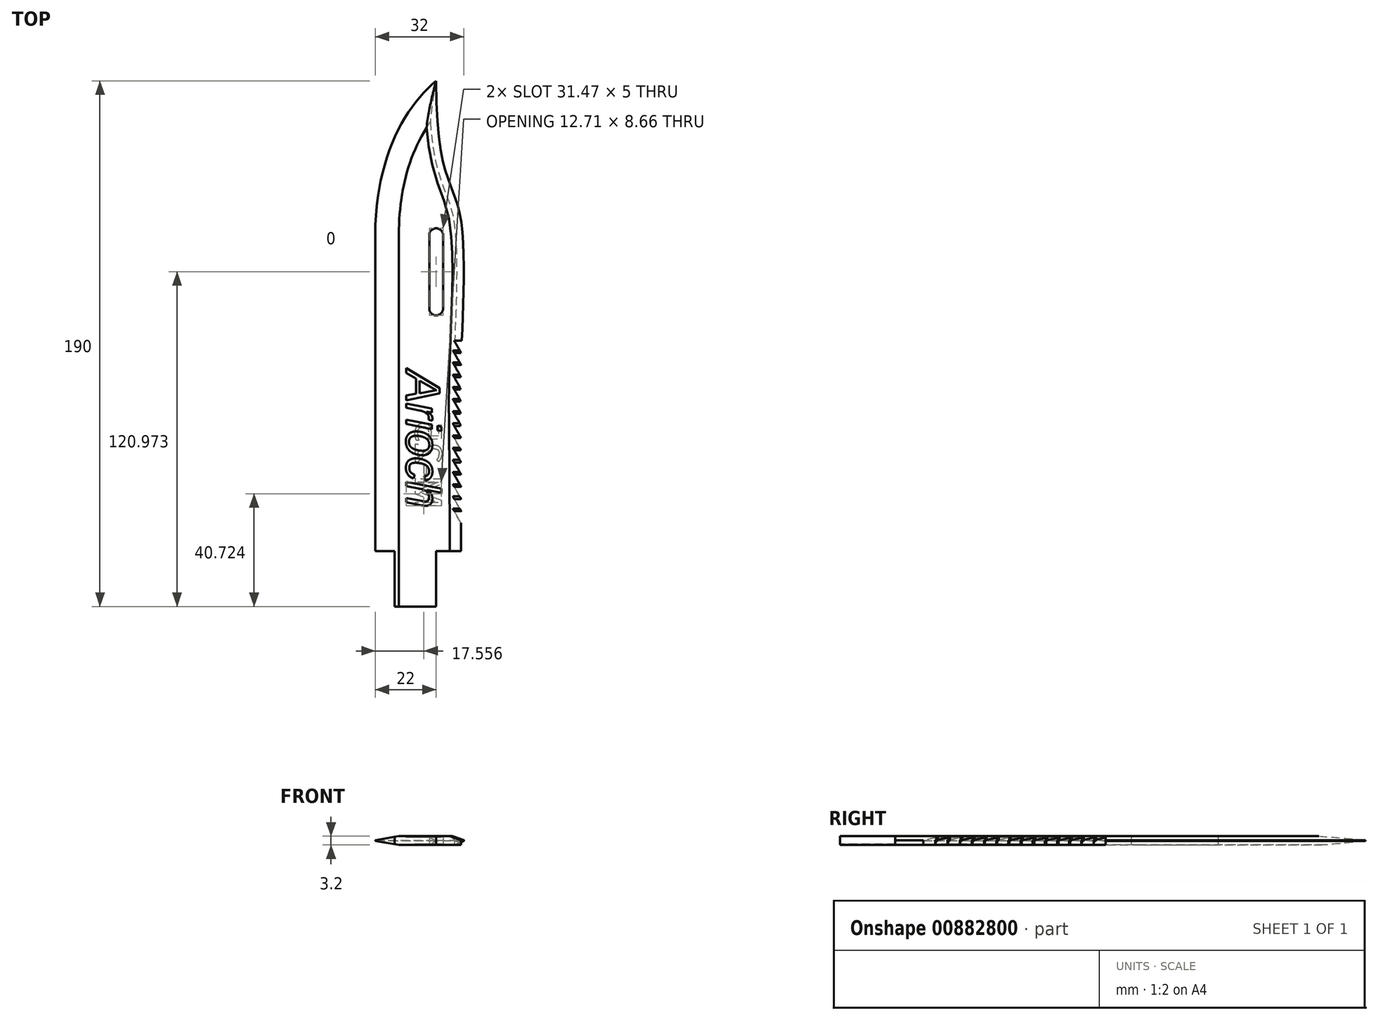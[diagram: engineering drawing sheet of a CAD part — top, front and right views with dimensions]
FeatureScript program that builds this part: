
annotation { "Feature Type Name" : "Feature", "Feature Type Description" : "" }
export const myFeature = defineFeature(function(context is Context, id is Id, definition is map)
    precondition{}
    {
        {
            var Q0;
            Q0=qCreatedBy(makeId("Top.planeOp"),FACE);
            var sketch = newSketch(context, id + "F0", { "sketchPlane" : qUnion([Q0])});
            skLineSegment(sketch, "E0", {"start": v(0, 138.73) * mm, "end": v(0, -81.27) * mm, "construction": true});
            skLineSegment(sketch, "E1", {"start": v(-22, -31.27) * mm, "end": v(9, -31.27) * mm, "construction": true});
            skLineSegment(sketch, "E2", {"start": v(-15, -31.27) * mm, "end": v(-15, -79.27) * mm});
            skLineSegment(sketch, "E3", {"start": v(0, -31.27) * mm, "end": v(0, -78.27) * mm});
            skLineSegment(sketch, "E4", {"start": v(-13, -81.27) * mm, "end": v(-3, -81.27) * mm});
            skPoint(sketch, "E5.visualSharp", {"position": v(0, -81.27) * mm});
            skArc(sketch, "E5.filletArc", {"start": v(-3, -81.27) * mm, "mid": v(-0.88, -80.39) * mm, "end": v(0, -78.27) * mm});
            skPoint(sketch, "E6.visualSharp", {"position": v(-15, -81.27) * mm});
            skArc(sketch, "E6.filletArc", {"start": v(-15, -79.27) * mm, "mid": v(-14.41, -80.68) * mm, "end": v(-13, -81.27) * mm});
            skLineSegment(sketch, "E7", {"start": v(9, -31.27) * mm, "end": v(9, 122.8) * mm, "construction": true});
            skLineSegment(sketch, "E8", {"start": v(-22, -31.27) * mm, "end": v(-22, 123.89) * mm, "construction": true});
            skLineSegment(sketch, "E9", {"start": v(-15, -31.27) * mm, "end": v(-22, -31.27) * mm});
            skLineSegment(sketch, "E10", {"start": v(0, -31.27) * mm, "end": v(9, -31.27) * mm});
            skLineSegment(sketch, "E11", {"start": v(-22, -31.27) * mm, "end": v(-22, 83.23) * mm});
            skFitSpline(sketch, "E12", {"points": [v(-22, 83.23) * mm, v(0, 138.73) * mm], "startDerivative": vector(0, 80.42) * mm, "endDerivative": vector(35.05, 28.76) * mm});
            skFitSpline(sketch, "E13", {"points": [v(0, 138.73) * mm, v(8.64, 90.14) * mm, v(9, 37.85) * mm, v(9, -31.27) * mm], "startDerivative": vector(0, -335.88) * mm, "endDerivative": vector(0, -393.77) * mm});
            skLineSegment(sketch, "E14", {"start": v(-8, -81.27) * mm, "end": v(-8, -31.27) * mm, "construction": true});
            skSolve(sketch);
        }
        {
            var Q0;
            Q0=qSketchRegion(id+"F0",true);
            extrude(context, id + "F1", {"entities" : qUnion([Q0]), "depth" : 3.2 * mm, "offsetDistance" : 25.4 * mm});
        }
        {
            var Q0;
            Q0=makeQuery(id+"F1.opExtrude","CAP_EDGE",EDGE,{"disambiguationData":[OSD([sQuery(id+"F0.wireOp",EDGE,"E11")])],"isStart":false});
            var Q1;
            Q1=makeQuery(id+"F1.opExtrude","CAP_EDGE",EDGE,{"disambiguationData":[OSD([sQuery(id+"F0.wireOp",EDGE,"E12")])],"isStart":false});
            chamfer(context, id + "F2", {"entities" : qUnion([Q0, Q1]), "chamferType" : ChamferType.OFFSET_ANGLE, "width" : 1.5 * mm, "oppositeDirection" : false, "angle" : 80 * degree, "tangentPropagation" : true});
        }
        {
            var Q0;
            Q0=makeQuery(id+"F1.opExtrude","CAP_EDGE",EDGE,{"disambiguationData":[OSD([sQuery(id+"F0.wireOp",EDGE,"E12")])],"isStart":true});
            chamfer(context, id + "F3", {"entities" : qUnion([Q0]), "chamferType" : ChamferType.OFFSET_ANGLE, "width" : 1.5 * mm, "oppositeDirection" : true, "angle" : 80 * degree, "tangentPropagation" : true});
        }
        {
            var Q0;
            Q0=makeQuery(id+"F1.opExtrude","CAP_FACE",FACE,{"disambiguationData":[OSD([sQuery(id+"F0.wireOp",EDGE,"E2"),sQuery(id+"F0.wireOp",EDGE,"E3"),sQuery(id+"F0.wireOp",EDGE,"E4"),sQuery(id+"F0.wireOp",EDGE,"E5.filletArc"),sQuery(id+"F0.wireOp",EDGE,"E6.filletArc"),sQuery(id+"F0.wireOp",EDGE,"E9"),sQuery(id+"F0.wireOp",EDGE,"E10"),sQuery(id+"F0.wireOp",EDGE,"E11"),sQuery(id+"F0.wireOp",EDGE,"E12"),sQuery(id+"F0.wireOp",EDGE,"E13")])],"isStart":true});
            var sketch = newSketch(context, id + "F4", { "sketchPlane" : qUnion([Q0])});
            skSolve(sketch);
        }
        {
            var Q0;
            {var subQ3=sQuery(id+"F0.wireOp",EDGE,"E10");Q0=makeQuery(id+"F4.imprint","IMPRINT",FACE,{"disambiguationData":[TD([[makeQuery(id+"F4.imprint","IMPRINT",EDGE,{"derivedFrom":makeQuery(id+"F1.opExtrude","CAP_EDGE",EDGE,{"disambiguationData":[OSD([subQ3])],"isStart":true})}),-1.0]])]});}
            var sketch = newSketch(context, id + "F5", { "sketchPlane" : qUnion([Q0])});
            skLineSegment(sketch, "E15", {"start": v(10.09, 23.07) * mm, "end": v(6.53, 16.8) * mm});
            skLineSegment(sketch, "E16", {"start": v(6.53, 16.8) * mm, "end": v(10.43, 16.8) * mm});
            skLineSegment(sketch, "E17", {"start": v(10.09, 23.07) * mm, "end": v(10.43, 16.8) * mm});
            skLineSegment(sketch, "E18.0.1.0", {"start": v(10.09, 18.67) * mm, "end": v(10.43, 12.4) * mm});
            skLineSegment(sketch, "E18.0.1.1", {"start": v(6.53, 12.4) * mm, "end": v(10.43, 12.4) * mm});
            skLineSegment(sketch, "E18.0.1.2", {"start": v(10.09, 18.67) * mm, "end": v(6.53, 12.4) * mm});
            skLineSegment(sketch, "E18.0.2.0", {"start": v(10.09, 14.27) * mm, "end": v(10.43, 8) * mm});
            skLineSegment(sketch, "E18.0.2.1", {"start": v(6.53, 8) * mm, "end": v(10.43, 8) * mm});
            skLineSegment(sketch, "E18.0.2.2", {"start": v(10.09, 14.27) * mm, "end": v(6.53, 8) * mm});
            skLineSegment(sketch, "E18.0.3.0", {"start": v(10.09, 9.87) * mm, "end": v(10.43, 3.6) * mm});
            skLineSegment(sketch, "E18.0.3.1", {"start": v(6.53, 3.6) * mm, "end": v(10.43, 3.6) * mm});
            skLineSegment(sketch, "E18.0.3.2", {"start": v(10.09, 9.87) * mm, "end": v(6.53, 3.6) * mm});
            skLineSegment(sketch, "E18.0.4.0", {"start": v(10.09, 5.47) * mm, "end": v(10.43, -0.8) * mm});
            skLineSegment(sketch, "E18.0.4.1", {"start": v(6.53, -0.8) * mm, "end": v(10.43, -0.8) * mm});
            skLineSegment(sketch, "E18.0.4.2", {"start": v(10.09, 5.47) * mm, "end": v(6.53, -0.8) * mm});
            skLineSegment(sketch, "E18.0.5.0", {"start": v(10.09, 1.07) * mm, "end": v(10.43, -5.2) * mm});
            skLineSegment(sketch, "E18.0.5.1", {"start": v(6.53, -5.2) * mm, "end": v(10.43, -5.2) * mm});
            skLineSegment(sketch, "E18.0.5.2", {"start": v(10.09, 1.07) * mm, "end": v(6.53, -5.2) * mm});
            skLineSegment(sketch, "E18.0.6.0", {"start": v(10.09, -3.33) * mm, "end": v(10.43, -9.6) * mm});
            skLineSegment(sketch, "E18.0.6.1", {"start": v(6.53, -9.6) * mm, "end": v(10.43, -9.6) * mm});
            skLineSegment(sketch, "E18.0.6.2", {"start": v(10.09, -3.33) * mm, "end": v(6.53, -9.6) * mm});
            skLineSegment(sketch, "E18.0.7.0", {"start": v(10.09, -7.73) * mm, "end": v(10.43, -14) * mm});
            skLineSegment(sketch, "E18.0.7.1", {"start": v(6.53, -14) * mm, "end": v(10.43, -14) * mm});
            skLineSegment(sketch, "E18.0.7.2", {"start": v(10.09, -7.73) * mm, "end": v(6.53, -14) * mm});
            skLineSegment(sketch, "E18.0.8.0", {"start": v(10.09, -12.13) * mm, "end": v(10.43, -18.4) * mm});
            skLineSegment(sketch, "E18.0.8.1", {"start": v(6.53, -18.4) * mm, "end": v(10.43, -18.4) * mm});
            skLineSegment(sketch, "E18.0.8.2", {"start": v(10.09, -12.13) * mm, "end": v(6.53, -18.4) * mm});
            skLineSegment(sketch, "E18.0.9.0", {"start": v(10.09, -16.53) * mm, "end": v(10.43, -22.8) * mm});
            skLineSegment(sketch, "E18.0.9.1", {"start": v(6.53, -22.8) * mm, "end": v(10.43, -22.8) * mm});
            skLineSegment(sketch, "E18.0.9.2", {"start": v(10.09, -16.53) * mm, "end": v(6.53, -22.8) * mm});
            skLineSegment(sketch, "E18.direction1", {"start": v(6.53, 16.8) * mm, "end": v(32.82, 16.8) * mm, "construction": true});
            skLineSegment(sketch, "E18.direction2", {"start": v(6.53, 16.8) * mm, "end": v(6.53, 12.4) * mm, "construction": true});
            skLineSegment(sketch, "E19.0.0.10", {"start": v(10.09, -20.93) * mm, "end": v(10.43, -27.2) * mm});
            skLineSegment(sketch, "E19.3.0.10", {"start": v(6.53, -27.2) * mm, "end": v(10.43, -27.2) * mm});
            skLineSegment(sketch, "E19.6.0.10", {"start": v(10.09, -20.93) * mm, "end": v(6.53, -27.2) * mm});
            skLineSegment(sketch, "E19.0.0.11", {"start": v(10.09, -25.33) * mm, "end": v(10.43, -31.6) * mm});
            skLineSegment(sketch, "E19.3.0.11", {"start": v(6.53, -31.6) * mm, "end": v(10.43, -31.6) * mm});
            skLineSegment(sketch, "E19.6.0.11", {"start": v(10.09, -25.33) * mm, "end": v(6.53, -31.6) * mm});
            skLineSegment(sketch, "E19.0.0.12", {"start": v(10.09, -29.73) * mm, "end": v(10.43, -36) * mm});
            skLineSegment(sketch, "E19.3.0.12", {"start": v(6.53, -36) * mm, "end": v(10.43, -36) * mm});
            skLineSegment(sketch, "E19.6.0.12", {"start": v(10.09, -29.73) * mm, "end": v(6.53, -36) * mm});
            skLineSegment(sketch, "E19.0.0.13", {"start": v(10.09, -34.13) * mm, "end": v(10.43, -40.4) * mm});
            skLineSegment(sketch, "E19.3.0.13", {"start": v(6.53, -40.4) * mm, "end": v(10.43, -40.4) * mm});
            skLineSegment(sketch, "E19.6.0.13", {"start": v(10.09, -34.13) * mm, "end": v(6.53, -40.4) * mm});
            skLineSegment(sketch, "E19.0.0.14", {"start": v(10.09, -38.53) * mm, "end": v(10.43, -44.8) * mm});
            skLineSegment(sketch, "E19.3.0.14", {"start": v(6.53, -44.8) * mm, "end": v(10.43, -44.8) * mm});
            skLineSegment(sketch, "E19.6.0.14", {"start": v(10.09, -38.53) * mm, "end": v(6.53, -44.8) * mm});
            skSolve(sketch);
        }
        {
            var Q0;
            Q0=qSketchRegion(id+"F5",true);
            extrude(context, id + "F6", {"entities" : qUnion([Q0]), "operationType" : NewBodyOperationType.REMOVE, "oppositeDirection" : true, "depth" : 25 * mm, "offsetDistance" : 25 * mm});
        }
        {
            var Q0;
            {var subQ3=sQuery(id+"F0.wireOp",EDGE,"E10");Q0=makeQuery(id+"F4.imprint","IMPRINT",FACE,{"disambiguationData":[TD([[makeQuery(id+"F4.imprint","IMPRINT",EDGE,{"derivedFrom":makeQuery(id+"F1.opExtrude","CAP_EDGE",EDGE,{"disambiguationData":[OSD([subQ3])],"isStart":true})}),-1.0]])]});}
            var sketch = newSketch(context, id + "F7", { "sketchPlane" : qUnion([Q0])});
            skLineSegment(sketch, "E20", {"start": v(0, -56.47) * mm, "end": v(0, -82.94) * mm, "construction": true});
            skArc(sketch, "E21.0.startCap", {"start": v(-2.5, -56.47) * mm, "mid": v(0, -53.97) * mm, "end": v(2.5, -56.47) * mm});
            skArc(sketch, "E21.0.endCap", {"start": v(2.5, -82.94) * mm, "mid": v(0, -85.44) * mm, "end": v(-2.5, -82.94) * mm});
            skLineSegment(sketch, "E21.0.left", {"start": v(2.5, -56.47) * mm, "end": v(2.5, -82.94) * mm});
            skLineSegment(sketch, "E21.0.right", {"start": v(-2.5, -56.47) * mm, "end": v(-2.5, -82.94) * mm});
            skSolve(sketch);
        }
        {
            var Q0;
            Q0=qSketchRegion(id+"F7",true);
            extrude(context, id + "F8", {"entities" : qUnion([Q0]), "operationType" : NewBodyOperationType.REMOVE, "oppositeDirection" : true, "depth" : 25 * mm, "offsetDistance" : 25 * mm});
        }
        {
            var Q0;
            {var subQ0=sQuery(id+"F0.wireOp",EDGE,"E13");var subQ1=sQuery(id+"F0.wireOp",EDGE,"E12");Q0=makeQuery(id+"F6.boolean.opBoolean","SPLIT",EDGE,{"disambiguationData":[TD([makeQuery(id+"F3.opChamfer","BLEND_FACE",FACE,{"disambiguationData":[OSD([subQ1])]})])],"derivedFrom":makeQuery(id+"F1.opExtrude","CAP_EDGE",EDGE,{"disambiguationData":[OSD([subQ0])],"isStart":true})});}
            chamfer(context, id + "F9", {"entities" : qUnion([Q0]), "chamferType" : ChamferType.OFFSET_ANGLE, "width" : 1.5 * mm, "oppositeDirection" : true, "angle" : 60 * degree, "tangentPropagation" : true});
        }
        {
            var Q0;
            {var subQ0=sQuery(id+"F0.wireOp",EDGE,"E13");var subQ1=sQuery(id+"F0.wireOp",EDGE,"E12");Q0=makeQuery(id+"F6.boolean.opBoolean","SPLIT",EDGE,{"disambiguationData":[TD([makeQuery(id+"F2.opChamfer","BLEND_FACE",FACE,{"disambiguationData":[OSD([subQ1])]})])],"derivedFrom":makeQuery(id+"F1.opExtrude","CAP_EDGE",EDGE,{"disambiguationData":[OSD([subQ0])],"isStart":false})});}
            chamfer(context, id + "F10", {"entities" : qUnion([Q0]), "chamferType" : ChamferType.OFFSET_ANGLE, "width" : 1.5 * mm, "oppositeDirection" : false, "angle" : 70 * degree, "tangentPropagation" : true});
        }
        {
            var Q0;
            {var subQ0=sQuery(id+"F0.wireOp",EDGE,"E13");var subQ1=sQuery(id+"F0.wireOp",EDGE,"E12");Q0=makeQuery(id+"F10.opChamfer","BLEND_EDGE",EDGE,{"blendedFrom":[makeQuery(id+"F6.boolean.opBoolean","SPLIT",EDGE,{"disambiguationData":[TD([makeQuery(id+"F2.opChamfer","BLEND_FACE",FACE,{"disambiguationData":[OSD([subQ1])]})])],"derivedFrom":makeQuery(id+"F1.opExtrude","CAP_EDGE",EDGE,{"disambiguationData":[OSD([subQ0])],"isStart":false})}),makeQuery(id+"F6.boolean.opBoolean","COPY",FACE,{"derivedFrom":makeQuery(id+"F6.opExtrude","SWEPT_FACE",FACE,{"disambiguationData":[OSD([sQuery(id+"F5.wireOp",EDGE,"E19.3.0.13")])]})})],"blendedInto":[makeQuery(id+"F6.boolean.opBoolean","COPY",FACE,{"derivedFrom":makeQuery(id+"F6.opExtrude","SWEPT_FACE",FACE,{"disambiguationData":[OSD([sQuery(id+"F5.wireOp",EDGE,"E19.3.0.13")])]})})]});}
            var Q1;
            {var subQ0=sQuery(id+"F0.wireOp",EDGE,"E13");var subQ1=sQuery(id+"F0.wireOp",EDGE,"E12");Q1=makeQuery(id+"F10.opChamfer","BLEND_EDGE",EDGE,{"blendedFrom":[makeQuery(id+"F6.boolean.opBoolean","SPLIT",EDGE,{"disambiguationData":[TD([makeQuery(id+"F2.opChamfer","BLEND_FACE",FACE,{"disambiguationData":[OSD([subQ1])]})])],"derivedFrom":makeQuery(id+"F1.opExtrude","CAP_EDGE",EDGE,{"disambiguationData":[OSD([subQ0])],"isStart":false})}),makeQuery(id+"F6.boolean.opBoolean","COPY",FACE,{"derivedFrom":makeQuery(id+"F6.opExtrude","SWEPT_FACE",FACE,{"disambiguationData":[OSD([sQuery(id+"F5.wireOp",EDGE,"E19.3.0.12")])]})})],"blendedInto":[makeQuery(id+"F6.boolean.opBoolean","COPY",FACE,{"derivedFrom":makeQuery(id+"F6.opExtrude","SWEPT_FACE",FACE,{"disambiguationData":[OSD([sQuery(id+"F5.wireOp",EDGE,"E19.3.0.12")])]})})]});}
            var Q2;
            {var subQ0=sQuery(id+"F0.wireOp",EDGE,"E13");var subQ1=sQuery(id+"F0.wireOp",EDGE,"E12");Q2=makeQuery(id+"F10.opChamfer","BLEND_EDGE",EDGE,{"blendedFrom":[makeQuery(id+"F6.boolean.opBoolean","SPLIT",EDGE,{"disambiguationData":[TD([makeQuery(id+"F2.opChamfer","BLEND_FACE",FACE,{"disambiguationData":[OSD([subQ1])]})])],"derivedFrom":makeQuery(id+"F1.opExtrude","CAP_EDGE",EDGE,{"disambiguationData":[OSD([subQ0])],"isStart":false})}),makeQuery(id+"F6.boolean.opBoolean","COPY",FACE,{"derivedFrom":makeQuery(id+"F6.opExtrude","SWEPT_FACE",FACE,{"disambiguationData":[OSD([sQuery(id+"F5.wireOp",EDGE,"E19.3.0.11")])]})})],"blendedInto":[makeQuery(id+"F6.boolean.opBoolean","COPY",FACE,{"derivedFrom":makeQuery(id+"F6.opExtrude","SWEPT_FACE",FACE,{"disambiguationData":[OSD([sQuery(id+"F5.wireOp",EDGE,"E19.3.0.11")])]})})]});}
            var Q3;
            {var subQ0=sQuery(id+"F0.wireOp",EDGE,"E13");var subQ1=sQuery(id+"F0.wireOp",EDGE,"E12");Q3=makeQuery(id+"F10.opChamfer","BLEND_EDGE",EDGE,{"blendedFrom":[makeQuery(id+"F6.boolean.opBoolean","SPLIT",EDGE,{"disambiguationData":[TD([makeQuery(id+"F2.opChamfer","BLEND_FACE",FACE,{"disambiguationData":[OSD([subQ1])]})])],"derivedFrom":makeQuery(id+"F1.opExtrude","CAP_EDGE",EDGE,{"disambiguationData":[OSD([subQ0])],"isStart":false})}),makeQuery(id+"F6.boolean.opBoolean","COPY",FACE,{"derivedFrom":makeQuery(id+"F6.opExtrude","SWEPT_FACE",FACE,{"disambiguationData":[OSD([sQuery(id+"F5.wireOp",EDGE,"E19.3.0.10")])]})})],"blendedInto":[makeQuery(id+"F6.boolean.opBoolean","COPY",FACE,{"derivedFrom":makeQuery(id+"F6.opExtrude","SWEPT_FACE",FACE,{"disambiguationData":[OSD([sQuery(id+"F5.wireOp",EDGE,"E19.3.0.10")])]})})]});}
            var Q4;
            {var subQ0=sQuery(id+"F0.wireOp",EDGE,"E13");var subQ1=sQuery(id+"F0.wireOp",EDGE,"E12");Q4=makeQuery(id+"F10.opChamfer","BLEND_EDGE",EDGE,{"blendedFrom":[makeQuery(id+"F6.boolean.opBoolean","SPLIT",EDGE,{"disambiguationData":[TD([makeQuery(id+"F2.opChamfer","BLEND_FACE",FACE,{"disambiguationData":[OSD([subQ1])]})])],"derivedFrom":makeQuery(id+"F1.opExtrude","CAP_EDGE",EDGE,{"disambiguationData":[OSD([subQ0])],"isStart":false})}),makeQuery(id+"F6.boolean.opBoolean","COPY",FACE,{"derivedFrom":makeQuery(id+"F6.opExtrude","SWEPT_FACE",FACE,{"disambiguationData":[OSD([sQuery(id+"F5.wireOp",EDGE,"E18.0.9.1")])]})})],"blendedInto":[makeQuery(id+"F6.boolean.opBoolean","COPY",FACE,{"derivedFrom":makeQuery(id+"F6.opExtrude","SWEPT_FACE",FACE,{"disambiguationData":[OSD([sQuery(id+"F5.wireOp",EDGE,"E18.0.9.1")])]})})]});}
            var Q5;
            {var subQ0=sQuery(id+"F0.wireOp",EDGE,"E13");var subQ1=sQuery(id+"F0.wireOp",EDGE,"E12");Q5=makeQuery(id+"F10.opChamfer","BLEND_EDGE",EDGE,{"blendedFrom":[makeQuery(id+"F6.boolean.opBoolean","SPLIT",EDGE,{"disambiguationData":[TD([makeQuery(id+"F2.opChamfer","BLEND_FACE",FACE,{"disambiguationData":[OSD([subQ1])]})])],"derivedFrom":makeQuery(id+"F1.opExtrude","CAP_EDGE",EDGE,{"disambiguationData":[OSD([subQ0])],"isStart":false})}),makeQuery(id+"F6.boolean.opBoolean","COPY",FACE,{"derivedFrom":makeQuery(id+"F6.opExtrude","SWEPT_FACE",FACE,{"disambiguationData":[OSD([sQuery(id+"F5.wireOp",EDGE,"E18.0.8.1")])]})})],"blendedInto":[makeQuery(id+"F6.boolean.opBoolean","COPY",FACE,{"derivedFrom":makeQuery(id+"F6.opExtrude","SWEPT_FACE",FACE,{"disambiguationData":[OSD([sQuery(id+"F5.wireOp",EDGE,"E18.0.8.1")])]})})]});}
            var Q6;
            {var subQ0=sQuery(id+"F0.wireOp",EDGE,"E13");var subQ1=sQuery(id+"F0.wireOp",EDGE,"E12");Q6=makeQuery(id+"F10.opChamfer","BLEND_EDGE",EDGE,{"blendedFrom":[makeQuery(id+"F6.boolean.opBoolean","SPLIT",EDGE,{"disambiguationData":[TD([makeQuery(id+"F2.opChamfer","BLEND_FACE",FACE,{"disambiguationData":[OSD([subQ1])]})])],"derivedFrom":makeQuery(id+"F1.opExtrude","CAP_EDGE",EDGE,{"disambiguationData":[OSD([subQ0])],"isStart":false})}),makeQuery(id+"F6.boolean.opBoolean","COPY",FACE,{"derivedFrom":makeQuery(id+"F6.opExtrude","SWEPT_FACE",FACE,{"disambiguationData":[OSD([sQuery(id+"F5.wireOp",EDGE,"E18.0.7.1")])]})})],"blendedInto":[makeQuery(id+"F6.boolean.opBoolean","COPY",FACE,{"derivedFrom":makeQuery(id+"F6.opExtrude","SWEPT_FACE",FACE,{"disambiguationData":[OSD([sQuery(id+"F5.wireOp",EDGE,"E18.0.7.1")])]})})]});}
            var Q7;
            {var subQ0=sQuery(id+"F0.wireOp",EDGE,"E13");var subQ1=sQuery(id+"F0.wireOp",EDGE,"E12");Q7=makeQuery(id+"F10.opChamfer","BLEND_EDGE",EDGE,{"blendedFrom":[makeQuery(id+"F6.boolean.opBoolean","SPLIT",EDGE,{"disambiguationData":[TD([makeQuery(id+"F2.opChamfer","BLEND_FACE",FACE,{"disambiguationData":[OSD([subQ1])]})])],"derivedFrom":makeQuery(id+"F1.opExtrude","CAP_EDGE",EDGE,{"disambiguationData":[OSD([subQ0])],"isStart":false})}),makeQuery(id+"F6.boolean.opBoolean","COPY",FACE,{"derivedFrom":makeQuery(id+"F6.opExtrude","SWEPT_FACE",FACE,{"disambiguationData":[OSD([sQuery(id+"F5.wireOp",EDGE,"E18.0.6.1")])]})})],"blendedInto":[makeQuery(id+"F6.boolean.opBoolean","COPY",FACE,{"derivedFrom":makeQuery(id+"F6.opExtrude","SWEPT_FACE",FACE,{"disambiguationData":[OSD([sQuery(id+"F5.wireOp",EDGE,"E18.0.6.1")])]})})]});}
            var Q8;
            {var subQ0=sQuery(id+"F0.wireOp",EDGE,"E13");var subQ1=sQuery(id+"F0.wireOp",EDGE,"E12");Q8=makeQuery(id+"F10.opChamfer","BLEND_EDGE",EDGE,{"blendedFrom":[makeQuery(id+"F6.boolean.opBoolean","SPLIT",EDGE,{"disambiguationData":[TD([makeQuery(id+"F2.opChamfer","BLEND_FACE",FACE,{"disambiguationData":[OSD([subQ1])]})])],"derivedFrom":makeQuery(id+"F1.opExtrude","CAP_EDGE",EDGE,{"disambiguationData":[OSD([subQ0])],"isStart":false})}),makeQuery(id+"F6.boolean.opBoolean","COPY",FACE,{"derivedFrom":makeQuery(id+"F6.opExtrude","SWEPT_FACE",FACE,{"disambiguationData":[OSD([sQuery(id+"F5.wireOp",EDGE,"E18.0.5.1")])]})})],"blendedInto":[makeQuery(id+"F6.boolean.opBoolean","COPY",FACE,{"derivedFrom":makeQuery(id+"F6.opExtrude","SWEPT_FACE",FACE,{"disambiguationData":[OSD([sQuery(id+"F5.wireOp",EDGE,"E18.0.5.1")])]})})]});}
            var Q9;
            {var subQ0=sQuery(id+"F0.wireOp",EDGE,"E13");var subQ1=sQuery(id+"F0.wireOp",EDGE,"E12");Q9=makeQuery(id+"F10.opChamfer","BLEND_EDGE",EDGE,{"blendedFrom":[makeQuery(id+"F6.boolean.opBoolean","SPLIT",EDGE,{"disambiguationData":[TD([makeQuery(id+"F2.opChamfer","BLEND_FACE",FACE,{"disambiguationData":[OSD([subQ1])]})])],"derivedFrom":makeQuery(id+"F1.opExtrude","CAP_EDGE",EDGE,{"disambiguationData":[OSD([subQ0])],"isStart":false})}),makeQuery(id+"F6.boolean.opBoolean","COPY",FACE,{"derivedFrom":makeQuery(id+"F6.opExtrude","SWEPT_FACE",FACE,{"disambiguationData":[OSD([sQuery(id+"F5.wireOp",EDGE,"E18.0.4.1")])]})})],"blendedInto":[makeQuery(id+"F6.boolean.opBoolean","COPY",FACE,{"derivedFrom":makeQuery(id+"F6.opExtrude","SWEPT_FACE",FACE,{"disambiguationData":[OSD([sQuery(id+"F5.wireOp",EDGE,"E18.0.4.1")])]})})]});}
            var Q10;
            {var subQ0=sQuery(id+"F0.wireOp",EDGE,"E13");var subQ1=sQuery(id+"F0.wireOp",EDGE,"E12");Q10=makeQuery(id+"F10.opChamfer","BLEND_EDGE",EDGE,{"blendedFrom":[makeQuery(id+"F6.boolean.opBoolean","SPLIT",EDGE,{"disambiguationData":[TD([makeQuery(id+"F2.opChamfer","BLEND_FACE",FACE,{"disambiguationData":[OSD([subQ1])]})])],"derivedFrom":makeQuery(id+"F1.opExtrude","CAP_EDGE",EDGE,{"disambiguationData":[OSD([subQ0])],"isStart":false})}),makeQuery(id+"F6.boolean.opBoolean","COPY",FACE,{"derivedFrom":makeQuery(id+"F6.opExtrude","SWEPT_FACE",FACE,{"disambiguationData":[OSD([sQuery(id+"F5.wireOp",EDGE,"E18.0.3.1")])]})})],"blendedInto":[makeQuery(id+"F6.boolean.opBoolean","COPY",FACE,{"derivedFrom":makeQuery(id+"F6.opExtrude","SWEPT_FACE",FACE,{"disambiguationData":[OSD([sQuery(id+"F5.wireOp",EDGE,"E18.0.3.1")])]})})]});}
            var Q11;
            {var subQ0=sQuery(id+"F0.wireOp",EDGE,"E13");var subQ1=sQuery(id+"F0.wireOp",EDGE,"E12");Q11=makeQuery(id+"F10.opChamfer","BLEND_EDGE",EDGE,{"blendedFrom":[makeQuery(id+"F6.boolean.opBoolean","SPLIT",EDGE,{"disambiguationData":[TD([makeQuery(id+"F2.opChamfer","BLEND_FACE",FACE,{"disambiguationData":[OSD([subQ1])]})])],"derivedFrom":makeQuery(id+"F1.opExtrude","CAP_EDGE",EDGE,{"disambiguationData":[OSD([subQ0])],"isStart":false})}),makeQuery(id+"F6.boolean.opBoolean","COPY",FACE,{"derivedFrom":makeQuery(id+"F6.opExtrude","SWEPT_FACE",FACE,{"disambiguationData":[OSD([sQuery(id+"F5.wireOp",EDGE,"E18.0.2.1")])]})})],"blendedInto":[makeQuery(id+"F6.boolean.opBoolean","COPY",FACE,{"derivedFrom":makeQuery(id+"F6.opExtrude","SWEPT_FACE",FACE,{"disambiguationData":[OSD([sQuery(id+"F5.wireOp",EDGE,"E18.0.2.1")])]})})]});}
            var Q12;
            {var subQ0=sQuery(id+"F0.wireOp",EDGE,"E13");var subQ1=sQuery(id+"F0.wireOp",EDGE,"E12");Q12=makeQuery(id+"F10.opChamfer","BLEND_EDGE",EDGE,{"blendedFrom":[makeQuery(id+"F6.boolean.opBoolean","SPLIT",EDGE,{"disambiguationData":[TD([makeQuery(id+"F2.opChamfer","BLEND_FACE",FACE,{"disambiguationData":[OSD([subQ1])]})])],"derivedFrom":makeQuery(id+"F1.opExtrude","CAP_EDGE",EDGE,{"disambiguationData":[OSD([subQ0])],"isStart":false})}),makeQuery(id+"F6.boolean.opBoolean","COPY",FACE,{"derivedFrom":makeQuery(id+"F6.opExtrude","SWEPT_FACE",FACE,{"disambiguationData":[OSD([sQuery(id+"F5.wireOp",EDGE,"E18.0.1.1")])]})})],"blendedInto":[makeQuery(id+"F6.boolean.opBoolean","COPY",FACE,{"derivedFrom":makeQuery(id+"F6.opExtrude","SWEPT_FACE",FACE,{"disambiguationData":[OSD([sQuery(id+"F5.wireOp",EDGE,"E18.0.1.1")])]})})]});}
            var Q13;
            {var subQ0=sQuery(id+"F0.wireOp",EDGE,"E13");var subQ1=sQuery(id+"F0.wireOp",EDGE,"E12");Q13=makeQuery(id+"F10.opChamfer","BLEND_EDGE",EDGE,{"blendedFrom":[makeQuery(id+"F6.boolean.opBoolean","SPLIT",EDGE,{"disambiguationData":[TD([makeQuery(id+"F2.opChamfer","BLEND_FACE",FACE,{"disambiguationData":[OSD([subQ1])]})])],"derivedFrom":makeQuery(id+"F1.opExtrude","CAP_EDGE",EDGE,{"disambiguationData":[OSD([subQ0])],"isStart":false})}),makeQuery(id+"F6.boolean.opBoolean","COPY",FACE,{"derivedFrom":makeQuery(id+"F6.opExtrude","SWEPT_FACE",FACE,{"disambiguationData":[OSD([sQuery(id+"F5.wireOp",EDGE,"E16")])]})})],"blendedInto":[makeQuery(id+"F6.boolean.opBoolean","COPY",FACE,{"derivedFrom":makeQuery(id+"F6.opExtrude","SWEPT_FACE",FACE,{"disambiguationData":[OSD([sQuery(id+"F5.wireOp",EDGE,"E16")])]})})]});}
            var Q14;
            Q14=makeQuery(id+"F6.boolean.opBoolean","COPY",EDGE,{"derivedFrom":makeQuery(id+"F6.opExtrude","CAP_EDGE",EDGE,{"disambiguationData":[OSD([sQuery(id+"F5.wireOp",EDGE,"E18.0.5.1")])],"isStart":true})});
            var Q15;
            Q15=makeQuery(id+"F6.boolean.opBoolean","COPY",EDGE,{"derivedFrom":makeQuery(id+"F6.opExtrude","CAP_EDGE",EDGE,{"disambiguationData":[OSD([sQuery(id+"F5.wireOp",EDGE,"E18.0.4.1")])],"isStart":true})});
            var Q16;
            Q16=makeQuery(id+"F6.boolean.opBoolean","COPY",EDGE,{"derivedFrom":makeQuery(id+"F6.opExtrude","CAP_EDGE",EDGE,{"disambiguationData":[OSD([sQuery(id+"F5.wireOp",EDGE,"E18.0.3.1")])],"isStart":true})});
            var Q17;
            Q17=makeQuery(id+"F6.boolean.opBoolean","COPY",EDGE,{"derivedFrom":makeQuery(id+"F6.opExtrude","CAP_EDGE",EDGE,{"disambiguationData":[OSD([sQuery(id+"F5.wireOp",EDGE,"E18.0.2.1")])],"isStart":true})});
            var Q18;
            Q18=makeQuery(id+"F6.boolean.opBoolean","COPY",EDGE,{"derivedFrom":makeQuery(id+"F6.opExtrude","CAP_EDGE",EDGE,{"disambiguationData":[OSD([sQuery(id+"F5.wireOp",EDGE,"E18.0.1.1")])],"isStart":true})});
            var Q19;
            Q19=makeQuery(id+"F6.boolean.opBoolean","COPY",EDGE,{"derivedFrom":makeQuery(id+"F6.opExtrude","CAP_EDGE",EDGE,{"disambiguationData":[OSD([sQuery(id+"F5.wireOp",EDGE,"E18.0.6.1")])],"isStart":true})});
            var Q20;
            Q20=makeQuery(id+"F6.boolean.opBoolean","COPY",EDGE,{"derivedFrom":makeQuery(id+"F6.opExtrude","CAP_EDGE",EDGE,{"disambiguationData":[OSD([sQuery(id+"F5.wireOp",EDGE,"E16")])],"isStart":true})});
            var Q21;
            Q21=makeQuery(id+"F6.boolean.opBoolean","COPY",EDGE,{"derivedFrom":makeQuery(id+"F6.opExtrude","CAP_EDGE",EDGE,{"disambiguationData":[OSD([sQuery(id+"F5.wireOp",EDGE,"E18.0.7.1")])],"isStart":true})});
            var Q22;
            Q22=makeQuery(id+"F6.boolean.opBoolean","COPY",EDGE,{"derivedFrom":makeQuery(id+"F6.opExtrude","CAP_EDGE",EDGE,{"disambiguationData":[OSD([sQuery(id+"F5.wireOp",EDGE,"E18.0.8.1")])],"isStart":true})});
            var Q23;
            Q23=makeQuery(id+"F6.boolean.opBoolean","COPY",EDGE,{"derivedFrom":makeQuery(id+"F6.opExtrude","CAP_EDGE",EDGE,{"disambiguationData":[OSD([sQuery(id+"F5.wireOp",EDGE,"E18.0.9.1")])],"isStart":true})});
            var Q24;
            Q24=makeQuery(id+"F6.boolean.opBoolean","COPY",EDGE,{"derivedFrom":makeQuery(id+"F6.opExtrude","CAP_EDGE",EDGE,{"disambiguationData":[OSD([sQuery(id+"F5.wireOp",EDGE,"E19.3.0.10")])],"isStart":true})});
            var Q25;
            Q25=makeQuery(id+"F6.boolean.opBoolean","COPY",EDGE,{"derivedFrom":makeQuery(id+"F6.opExtrude","CAP_EDGE",EDGE,{"disambiguationData":[OSD([sQuery(id+"F5.wireOp",EDGE,"E19.3.0.11")])],"isStart":true})});
            var Q26;
            Q26=makeQuery(id+"F6.boolean.opBoolean","COPY",EDGE,{"derivedFrom":makeQuery(id+"F6.opExtrude","CAP_EDGE",EDGE,{"disambiguationData":[OSD([sQuery(id+"F5.wireOp",EDGE,"E19.3.0.12")])],"isStart":true})});
            var Q27;
            Q27=makeQuery(id+"F6.boolean.opBoolean","COPY",EDGE,{"derivedFrom":makeQuery(id+"F6.opExtrude","CAP_EDGE",EDGE,{"disambiguationData":[OSD([sQuery(id+"F5.wireOp",EDGE,"E19.3.0.13")])],"isStart":true})});
            chamfer(context, id + "F11", {"entities" : qUnion([Q0, Q1, Q2, Q3, Q4, Q5, Q6, Q7, Q8, Q9, Q10, Q11, Q12, Q13, Q14, Q15, Q16, Q17, Q18, Q19, Q20, Q21, Q22, Q23, Q24, Q25, Q26, Q27]), "chamferType" : ChamferType.OFFSET_ANGLE, "width" : 0.9 * mm, "oppositeDirection" : false, "angle" : 45 * degree});
        }
        {
            var Q0;
            {var subQ3=sQuery(id+"F0.wireOp",EDGE,"E10");Q0=makeQuery(id+"F4.imprint","IMPRINT",FACE,{"disambiguationData":[TD([[makeQuery(id+"F4.imprint","IMPRINT",EDGE,{"derivedFrom":makeQuery(id+"F1.opExtrude","CAP_EDGE",EDGE,{"disambiguationData":[OSD([subQ3])],"isStart":true})}),-1.0]])]});}
            var sketch = newSketch(context, id + "F12", { "sketchPlane" : qUnion([Q0])});
            skText(sketch, "E22", { "text": "M-25", "fontName": "NotoSans-Regular.ttf"});
            const initialGuessF12  = {"E22": [-0.0076, 0.01609, 0, -1, 0.00964]};
            skSetInitialGuess(sketch, initialGuessF12);
            skSolve(sketch);
        }
        {
            var Q0;
            Q0=qSketchRegion(id+"F12",true);
            extrude(context, id + "F13", {"entities" : qUnion([Q0]), "operationType" : NewBodyOperationType.REMOVE, "oppositeDirection" : true, "depth" : 0.3 * mm, "offsetDistance" : 25 * mm});
        }
        {
            var Q0;
            Q0=makeQuery(id+"F1.opExtrude","CAP_FACE",FACE,{"disambiguationData":[OSD([sQuery(id+"F0.wireOp",EDGE,"E2"),sQuery(id+"F0.wireOp",EDGE,"E3"),sQuery(id+"F0.wireOp",EDGE,"E4"),sQuery(id+"F0.wireOp",EDGE,"E5.filletArc"),sQuery(id+"F0.wireOp",EDGE,"E6.filletArc"),sQuery(id+"F0.wireOp",EDGE,"E9"),sQuery(id+"F0.wireOp",EDGE,"E10"),sQuery(id+"F0.wireOp",EDGE,"E11"),sQuery(id+"F0.wireOp",EDGE,"E12"),sQuery(id+"F0.wireOp",EDGE,"E13"),sQuery(id+"F0.wireOp",EDGE,"E04xeWy3-CUXz-6SZ0-vJ5X-Rzi5LjpGnLXz"),sQuery(id+"F0.wireOp",EDGE,"WPopt2dh-tzsb-YNtA-skAR-ybRoaueNO6dU")])],"isStart":false});
            var sketch = newSketch(context, id + "F14", { "sketchPlane" : qUnion([Q0])});
            skText(sketch, "E23", { "text": "Arioch", "fontName": "Arimo-Italic.ttf"});
            const initialGuessF14  = {"E23": [-0.0108, 0.03404, 0, -1, 0.01263]};
            skSetInitialGuess(sketch, initialGuessF14);
            skSolve(sketch);
        }
        {
            var Q0;
            Q0=qSketchRegion(id+"F14",true);
            extrude(context, id + "F15", {"entities" : qUnion([Q0]), "operationType" : NewBodyOperationType.REMOVE, "oppositeDirection" : true, "depth" : 0.3 * mm, "offsetDistance" : 25 * mm});
        }
        {
            var Q0;
            Q0=qCreatedBy(makeId("Top.planeOp"),FACE);
            var sketch = newSketch(context, id + "F16", { "sketchPlane" : qUnion([Q0])});
            skLineSegment(sketch, "E24.bottom", {"start": v(-41.2, -51.27) * mm, "end": v(30.98, -51.27) * mm});
            skLineSegment(sketch, "E24.top", {"start": v(-41.2, -89.77) * mm, "end": v(30.98, -89.77) * mm});
            skLineSegment(sketch, "E24.left", {"start": v(-41.2, -51.27) * mm, "end": v(-41.2, -89.77) * mm});
            skLineSegment(sketch, "E24.right", {"start": v(30.98, -51.27) * mm, "end": v(30.98, -89.77) * mm});
            skSolve(sketch);
        }
        {
            var Q0;
            Q0 = qSketchRegion(id + "F16", true);
            extrude(context, id + "F17", {"entities" : qUnion([Q0]), "operationType" : NewBodyOperationType.REMOVE, "endBound" : BoundingType.SYMMETRIC, "oppositeDirection" : true, "depth" : 25 * mm, "offsetDistance" : 25 * mm});
        }
    });
